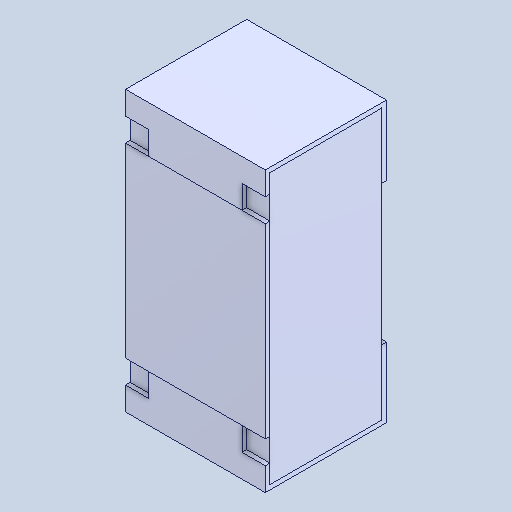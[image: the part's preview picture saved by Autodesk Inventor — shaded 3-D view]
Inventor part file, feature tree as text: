
AUTODESK INVENTOR PART (.ipt)
format: ipt  version: 2025 (Build 290162000, 162)  size: 111,616 bytes
history: native  units: mm
features: boolean_combine x2, other x1, mirror x1
ambient origin geometry x8: Origin, YZ Plane, XZ Plane, XY Plane, X Axis, Y Axis, Z Axis, Center Point
bodies: Solid1 (feature_tree), Solid2 (feature_tree), Solid3 (feature_tree), Solid4 (feature_tree)
feature tree (4):
  other  "Cut-Extrude1"
  boolean_combine  "Combine2"
  mirror  "Mirror1[3]"
  boolean_combine  "Combine1"
